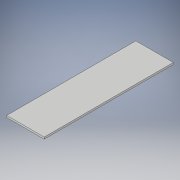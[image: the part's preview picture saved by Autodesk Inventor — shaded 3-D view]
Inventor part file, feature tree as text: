
AUTODESK INVENTOR PART (.ipt)
format: ipt  version: 2017 (Build 210142000, 142)  size: 89,600 bytes
history: native  units: in
note: dims shown in document units (in); Inventor stores cm internally (conversion verified against a paired STEP export)
features: extrude x1, sketch x1
ambient origin geometry x8: Origin, YZ Plane, XZ Plane, XY Plane, X Axis, Y Axis, Z Axis, Center Point
bodies: Solid1 (feature_tree)
feature tree (2):
  extrude  "Extrusion1"  Depth=17.5in
  sketch  "Sketch1"  dims[d0=5.075in d1=17.5in d2=0.25in d3=0.0in]
